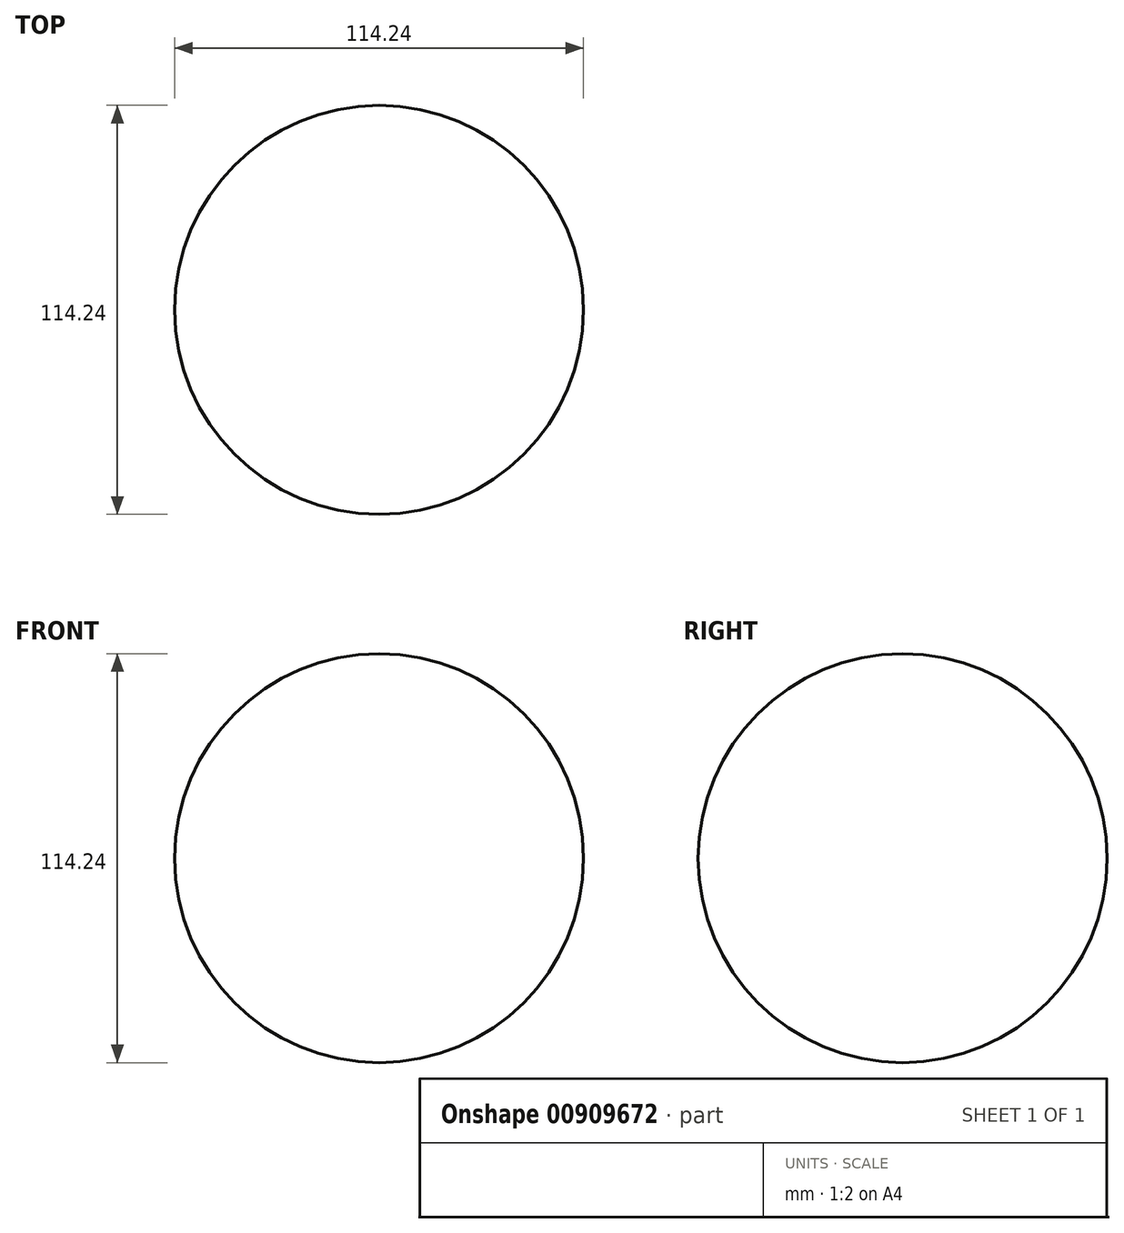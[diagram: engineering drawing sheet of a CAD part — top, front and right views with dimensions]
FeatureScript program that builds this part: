
annotation { "Feature Type Name" : "Feature", "Feature Type Description" : "" }
export const myFeature = defineFeature(function(context is Context, id is Id, definition is map)
    precondition{}
    {
        {
            var Q0;
            Q0=qCreatedBy(makeId("Front.planeOp"),FACE);
            var sketch = newSketch(context, id + "F0", { "sketchPlane" : qUnion([Q0])});
            skArc(sketch, "E0", {"start": v(0, -57.12) * mm, "mid": v(57.12, 0) * mm, "end": v(0, 57.12) * mm});
            skLineSegment(sketch, "E1", {"start": v(0, 68.38) * mm, "end": v(0, -69.06) * mm});
            skSolve(sketch);
        }
        {
            var Q0;
            {var subQ0=sQuery(id+"F0.wireOp",EDGE,"E0");Q0=makeQuery(id+"F0.imprint","IMPRINT",FACE,{"disambiguationData":[TD([[makeQuery(id+"F0.imprint","IMPRINT",EDGE,{"derivedFrom":subQ0}),1.0]])]});}
            var Q1;
            Q1=sQuery(id+"F0.wireOp",EDGE,"E1");
            revolve(context, id + "F1", {"surfaceOperationType" : NewSurfaceOperationType.NEW, "entities" : qUnion([Q0]), "axis" : qUnion([Q1]), "revolveType" : RevolveType.FULL});
        }
        {
            var Q0;
            Q0=qCreatedBy(makeId("Front.planeOp"),FACE);
            var sketch = newSketch(context, id + "F2", { "sketchPlane" : qUnion([Q0])});
            skCircle(sketch, "E2", {"center": v(0, 0) * mm, "radius": 5.74 * mm});
            skCircle(sketch, "E3", {"center": v(0, 0) * mm, "radius": 12.78 * mm});
            skCircle(sketch, "E4", {"center": v(0, 0) * mm, "radius": 45.8 * mm});
            skCircle(sketch, "E5", {"center": v(0, 0) * mm, "radius": 51.35 * mm});
            skCircle(sketch, "E6", {"center": v(0, 0) * mm, "radius": 41.17 * mm});
            skSolve(sketch);
        }
    });
